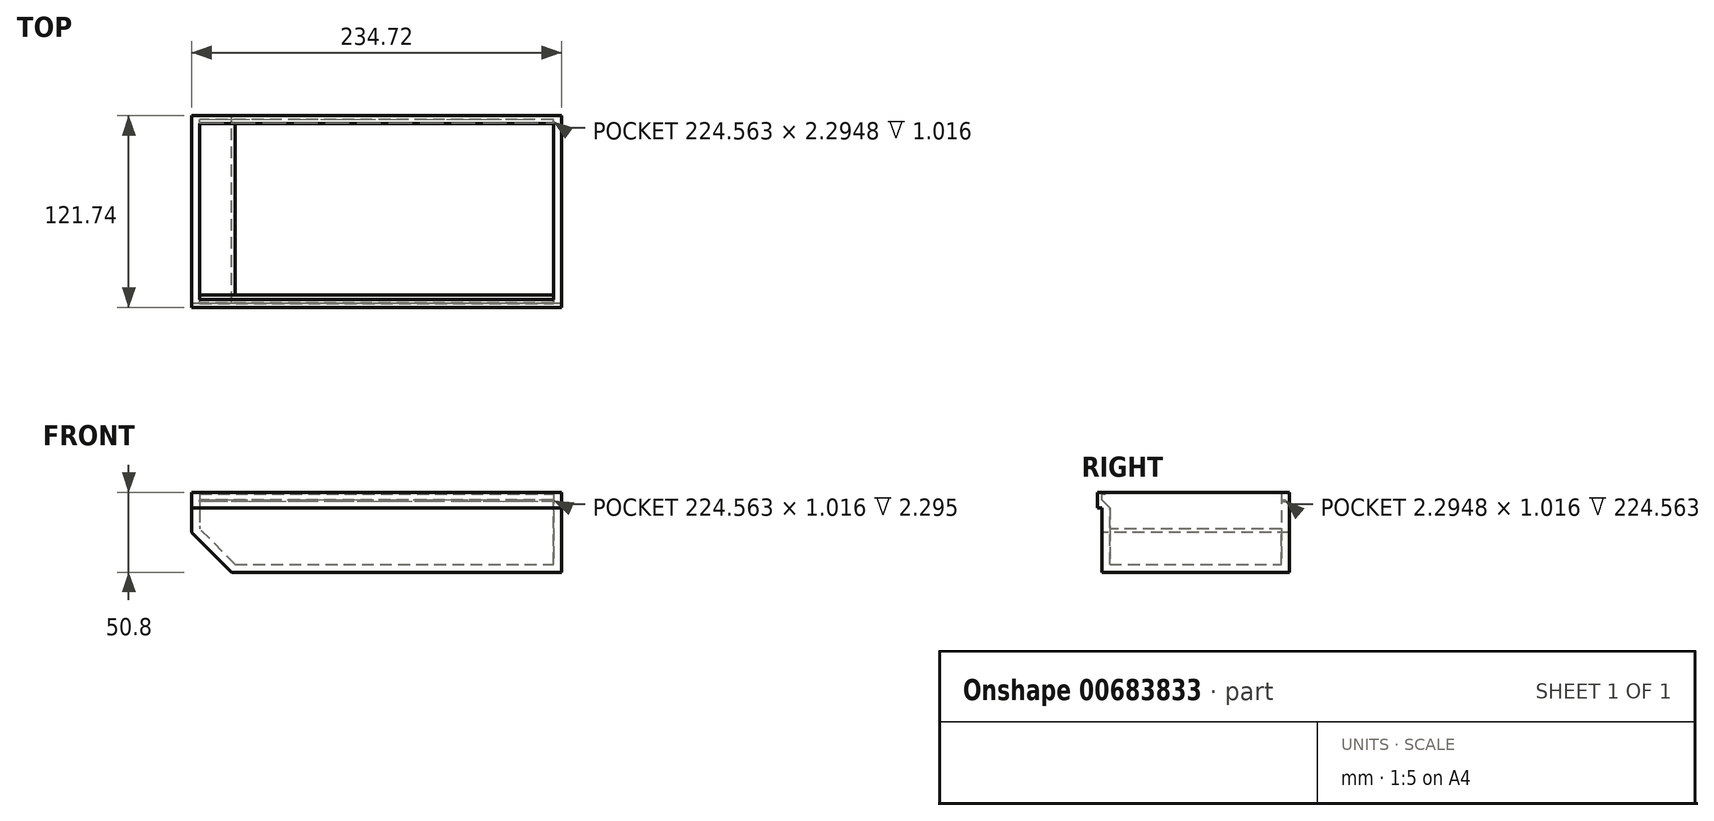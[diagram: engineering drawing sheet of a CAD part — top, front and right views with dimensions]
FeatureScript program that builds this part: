
annotation { "Feature Type Name" : "Feature", "Feature Type Description" : "" }
export const myFeature = defineFeature(function(context is Context, id is Id, definition is map)
    precondition{}
    {
        {
            var Q0;
            Q0=qCreatedBy(makeId("Top.planeOp"),FACE);
            var sketch = newSketch(context, id + "F0", { "sketchPlane" : qUnion([Q0])});
            skLineSegment(sketch, "E0.bottom", {"start": v(117.36, -60.87) * mm, "end": v(-117.36, -60.87) * mm});
            skLineSegment(sketch, "E0.top", {"start": v(117.36, 60.87) * mm, "end": v(-117.36, 60.87) * mm});
            skLineSegment(sketch, "E0.left", {"start": v(117.36, -60.87) * mm, "end": v(117.36, 60.87) * mm});
            skLineSegment(sketch, "E0.right", {"start": v(-117.36, -60.87) * mm, "end": v(-117.36, 60.87) * mm});
            skPoint(sketch, "E0.middle", {"position": v(0, 0) * mm});
            skSolve(sketch);
        }
        {
            var Q0;
            Q0=makeQuery(id+"F0.imprint","IMPRINT",FACE,{"disambiguationData":[TD([[makeQuery(id+"F0.imprint","IMPRINT",EDGE,{"derivedFrom":sQuery(id+"F0.wireOp",EDGE,"E0.bottom")}),-1.0]])]});
            extrude(context, id + "F1", {"entities" : qUnion([Q0]), "depth" : 25.4 * mm, "offsetDistance" : 25.4 * mm, "hasSecondDirection" : true, "secondDirectionOppositeDirection" : true, "secondDirectionDepth" : 25.4 * mm});
        }
        {
            var Q0;
            Q0=makeQuery(id+"F1.opExtrude","SWEPT_FACE",FACE,{"disambiguationData":[OSD([sQuery(id+"F0.wireOp",EDGE,"E0.left")])]});
            var sketch = newSketch(context, id + "F2", { "sketchPlane" : qUnion([Q0])});
            skLineSegment(sketch, "E1.bottom", {"start": v(-60.87, -25.4) * mm, "end": v(-58.19, -25.4) * mm});
            skLineSegment(sketch, "E1.top", {"start": v(-60.87, 15.6) * mm, "end": v(-58.19, 15.6) * mm});
            skLineSegment(sketch, "E1.left", {"start": v(-60.87, -25.4) * mm, "end": v(-60.87, 15.6) * mm});
            skLineSegment(sketch, "E1.right", {"start": v(-58.19, -25.4) * mm, "end": v(-58.19, 15.6) * mm});
            skSolve(sketch);
        }
        {
            var Q0;
            Q0=makeQuery(id+"F2.imprint","IMPRINT",FACE,{"disambiguationData":[TD([[makeQuery(id+"F2.imprint","IMPRINT",EDGE,{"derivedFrom":sQuery(id+"F2.wireOp",EDGE,"E1.bottom")}),1.0]])]});
            extrude(context, id + "F3", {"entities" : qUnion([Q0]), "operationType" : NewBodyOperationType.REMOVE, "oppositeDirection" : true, "depth" : 239.78 * mm, "offsetDistance" : 25.4 * mm});
        }
        {
            var Q0;
            Q0=makeQuery(id+"F1.opExtrude","CAP_EDGE",EDGE,{"disambiguationData":[OSD([sQuery(id+"F0.wireOp",EDGE,"E0.right")])],"isStart":true});
            chamfer(context, id + "F4", {"entities" : qUnion([Q0]), "width" : 25.4 * mm, "tangentPropagation" : true});
        }
        {
            var Q0;
            Q0=makeQuery(id+"F3.boolean.opBoolean","COPY",FACE,{"derivedFrom":makeQuery(id+"F3.opExtrude","SWEPT_FACE",FACE,{"disambiguationData":[OSD([sQuery(id+"F2.wireOp",EDGE,"E1.right")])]})});
            var sketch = newSketch(context, id + "F5", { "sketchPlane" : qUnion([Q0])});
            skLineSegment(sketch, "E2.bottom", {"start": v(117.36, 15.6) * mm, "end": v(106.14, 15.6) * mm});
            skLineSegment(sketch, "E2.top", {"start": v(117.36, -25.4) * mm, "end": v(106.14, -25.4) * mm});
            skLineSegment(sketch, "E2.left", {"start": v(117.36, 15.6) * mm, "end": v(117.36, -25.4) * mm});
            skLineSegment(sketch, "E2.right", {"start": v(106.14, 15.6) * mm, "end": v(106.14, -25.4) * mm});
            skSolve(sketch);
        }
        {
            var Q0;
            Q0=makeQuery(id+"F1.opExtrude","CAP_FACE",FACE,{"disambiguationData":[OSD([sQuery(id+"F0.wireOp",EDGE,"E0.bottom"),sQuery(id+"F0.wireOp",EDGE,"E0.top"),sQuery(id+"F0.wireOp",EDGE,"E0.left"),sQuery(id+"F0.wireOp",EDGE,"E0.right")])],"isStart":false});
            shell(context, id + "F6", {"entities" : qUnion([Q0]), "thickness" : 5.08 * mm});
        }
        {
            var Q0;
            Q0=makeQuery(id+"F6.opShell","OFFSET_FACE",FACE,{"disambiguationData":[OSD([sQuery(id+"F0.wireOp",EDGE,"E0.bottom")])]});
            var sketch = newSketch(context, id + "F7", { "sketchPlane" : qUnion([Q0])});
            skLineSegment(sketch, "E3.bottom", {"start": v(112.28, 20.68) * mm, "end": v(-112.28, 20.68) * mm});
            skLineSegment(sketch, "E3.top", {"start": v(112.28, 24.24) * mm, "end": v(-112.28, 24.24) * mm});
            skLineSegment(sketch, "E3.left", {"start": v(112.28, 20.68) * mm, "end": v(112.28, 24.24) * mm});
            skLineSegment(sketch, "E3.right", {"start": v(-112.28, 20.68) * mm, "end": v(-112.28, 24.24) * mm});
            skPoint(sketch, "E3.middle", {"position": v(0, 22.46) * mm});
            skPoint(sketch, "E3.middle.positionSnap0", {"position": v(0, 20.68) * mm});
            skPoint(sketch, "E3.centerSnap0", {"position": v(0, 20.68) * mm});
            skSolve(sketch);
        }
        {
            var Q0;
            Q0=makeQuery(id+"F7.imprint","IMPRINT",FACE,{"disambiguationData":[TD([[makeQuery(id+"F7.imprint","IMPRINT",EDGE,{"derivedFrom":sQuery(id+"F7.wireOp",EDGE,"E3.bottom")}),-1.0]])]});
            extrude(context, id + "F8", {"entities" : qUnion([Q0]), "operationType" : NewBodyOperationType.REMOVE, "oppositeDirection" : true, "depth" : 2.54 * mm, "offsetDistance" : 25.4 * mm});
        }
        {
            var Q0;
            {var subQ0=sQuery(id+"F7.wireOp",EDGE,"E3.bottom");Q0=makeQuery(id+"Fzltu2EiTvpH8gv_1.1.F8.boolean.opBoolean","MERGE",FACE,{"derivedFrom":[makeQuery(id+"F8.boolean.opBoolean","MERGE",FACE,{"derivedFrom":[makeQuery(id+"F6.opShell","OFFSET_FACE",FACE,{"disambiguationData":[OSD([sQuery(id+"F2.wireOp",EDGE,"E1.top"),sQuery(id+"F5.wireOp",EDGE,"E2.bottom")])]}),makeQuery(id+"F8.opExtrude","SWEPT_FACE",FACE,{"disambiguationData":[OSD([subQ0])]})]}),makeQuery(id+"Fzltu2EiTvpH8gv_1.1.F8.opExtrude","SWEPT_FACE",FACE,{"disambiguationData":[OSD([subQ0])]})]});}
            var sketch = newSketch(context, id + "F9", { "sketchPlane" : qUnion([Q0])});
            skLineSegment(sketch, "E4.bottom", {"start": v(112.28, 56.05) * mm, "end": v(-112.28, 56.05) * mm});
            skLineSegment(sketch, "E4.top", {"start": v(112.28, 58.34) * mm, "end": v(-112.28, 58.34) * mm});
            skLineSegment(sketch, "E4.left", {"start": v(112.28, 56.05) * mm, "end": v(112.28, 58.34) * mm});
            skLineSegment(sketch, "E4.right", {"start": v(-112.28, 56.05) * mm, "end": v(-112.28, 58.34) * mm});
            skPoint(sketch, "E4.middle", {"position": v(0, 57.2) * mm});
            skSolve(sketch);
        }
        {
            var Q0;
            {var subQ0=sQuery(id+"F9.wireOp",EDGE,"E4.bottom");Q0=makeQuery(id+"F9.imprint","IMPRINT",FACE,{"disambiguationData":[TD([[makeQuery(id+"F9.imprint","IMPRINT",EDGE,{"derivedFrom":subQ0}),-1.0]])]});}
            extrude(context, id + "F10", {"entities" : qUnion([Q0]), "operationType" : NewBodyOperationType.REMOVE, "oppositeDirection" : true, "depth" : 1.02 * mm, "offsetDistance" : 25.4 * mm});
        }
        {
            var Q0;
            {var subQ0=sQuery(id+"F5.wireOp",EDGE,"E2.right");var subQ1=sQuery(id+"F5.wireOp",EDGE,"E2.bottom");var subQ2=sQuery(id+"F2.wireOp",EDGE,"E1.right");var subQ3=sQuery(id+"F2.wireOp",EDGE,"E1.top");Q0=makeQuery(id+"F6.opShell","OFFSET_EDGE",EDGE,{"disambiguationData":[OSD([subQ3,subQ2,subQ1,subQ0]),TDD([makeQuery(id+"FAR787cbMJIEUEK_1.1.F0aL4B2t44WcTH9_1.boolean.opBoolean","COPY",EDGE,{"derivedFrom":makeQuery(id+"FAR787cbMJIEUEK_1.1.F0aL4B2t44WcTH9_1.opExtrude","SWEPT_EDGE",EDGE,{"disambiguationData":[OSD([subQ3,subQ2,subQ1,subQ0])]})})])]});}
            var Q1;
            {var subQ0=sQuery(id+"F2.wireOp",EDGE,"E1.right");var subQ1=sQuery(id+"F2.wireOp",EDGE,"E1.top");Q1=makeQuery(id+"F6.opShell","OFFSET_EDGE",EDGE,{"disambiguationData":[OSD([subQ1,subQ0]),TDD([makeQuery(id+"FwPR4XzUNfVJvJA_1.1.F3.boolean.opBoolean","COPY",EDGE,{"derivedFrom":makeQuery(id+"FwPR4XzUNfVJvJA_1.1.F3.opExtrude","SWEPT_EDGE",EDGE,{"disambiguationData":[OSD([subQ1,subQ0])]})})])]});}
            var Q2;
            {var subQ0=sQuery(id+"F2.wireOp",EDGE,"E1.right");var subQ1=sQuery(id+"F2.wireOp",EDGE,"E1.top");Q2=makeQuery(id+"F6.opShell","OFFSET_EDGE",EDGE,{"disambiguationData":[OSD([subQ1,subQ0]),TDD([makeQuery(id+"F3.boolean.opBoolean","COPY",EDGE,{"derivedFrom":makeQuery(id+"F3.opExtrude","SWEPT_EDGE",EDGE,{"disambiguationData":[OSD([subQ1,subQ0])]})})])]});}
            var Q3;
            {var subQ0=sQuery(id+"F5.wireOp",EDGE,"E2.right");var subQ1=sQuery(id+"F5.wireOp",EDGE,"E2.bottom");var subQ2=sQuery(id+"F2.wireOp",EDGE,"E1.right");var subQ3=sQuery(id+"F2.wireOp",EDGE,"E1.top");Q3=makeQuery(id+"F6.opShell","OFFSET_EDGE",EDGE,{"disambiguationData":[OSD([subQ3,subQ2,subQ1,subQ0]),TDD([makeQuery(id+"F0aL4B2t44WcTH9_1.boolean.opBoolean","COPY",EDGE,{"derivedFrom":makeQuery(id+"F0aL4B2t44WcTH9_1.opExtrude","SWEPT_EDGE",EDGE,{"disambiguationData":[OSD([subQ3,subQ2,subQ1,subQ0])]})})])]});}
            chamfer(context, id + "F11", {"entities" : qUnion([Q0, Q1, Q2, Q3]), "width" : 5.08 * mm, "tangentPropagation" : true});
        }
    });
